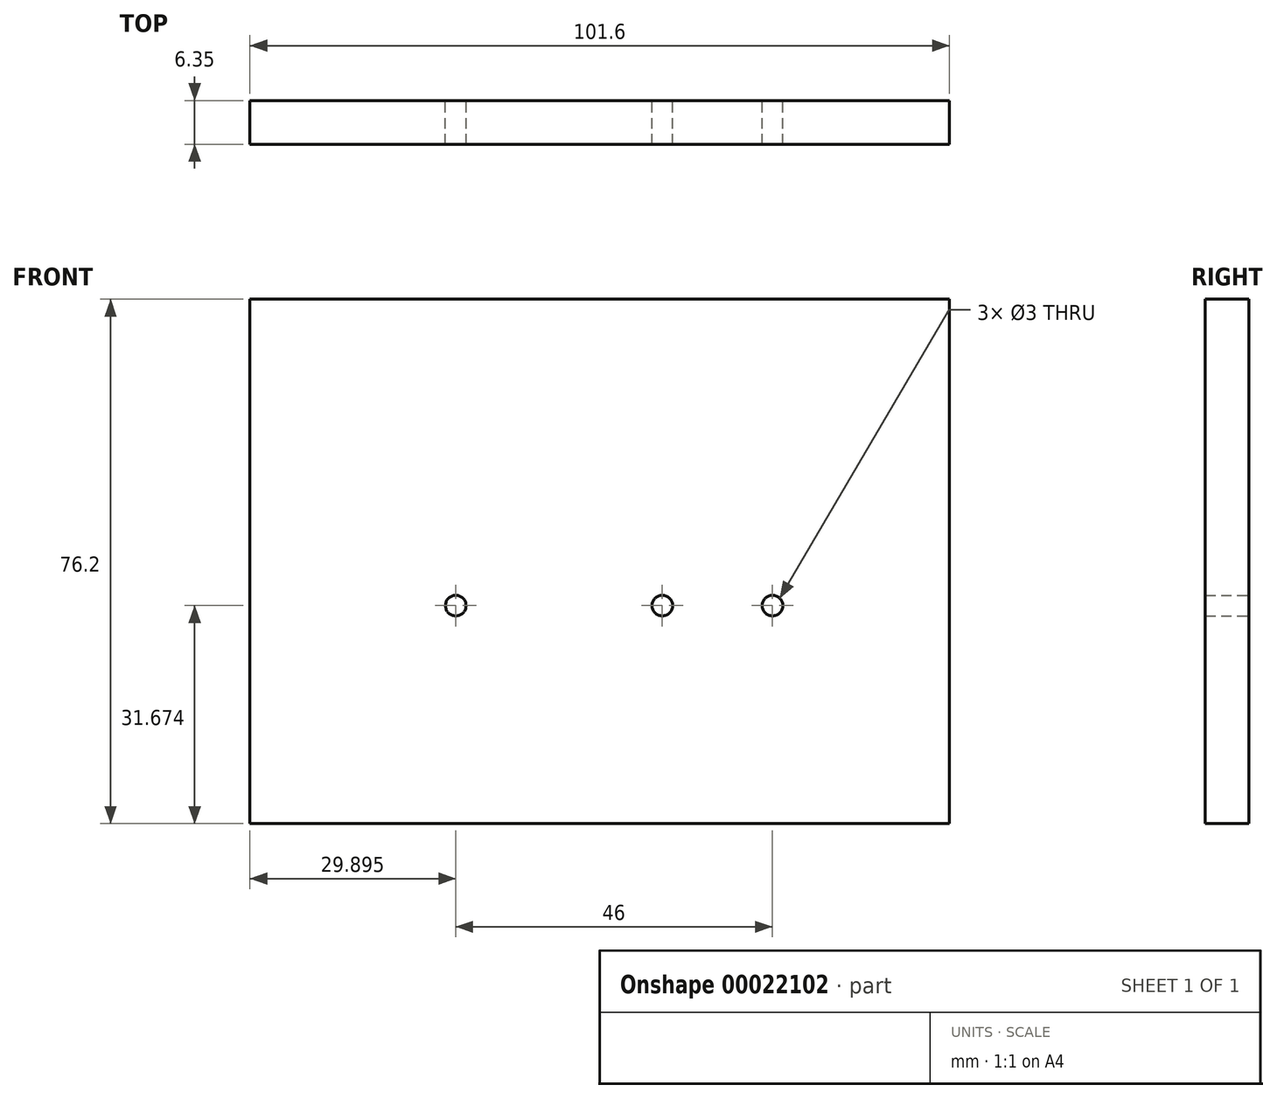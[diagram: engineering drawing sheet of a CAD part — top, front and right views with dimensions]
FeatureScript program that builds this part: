
annotation { "Feature Type Name" : "Feature", "Feature Type Description" : "" }
export const myFeature = defineFeature(function(context is Context, id is Id, definition is map)
    precondition{}
    {
        {
            var Q0;
            Q0=qCreatedBy(makeId("Front.planeOp"),FACE);
            var sketch = newSketch(context, id + "F0", { "sketchPlane" : qUnion([Q0])});
            skLineSegment(sketch, "E0.bottom", {"start": v(-44.9, 85) * mm, "end": v(56.7, 85) * mm});
            skLineSegment(sketch, "E0.top", {"start": v(-44.9, 8.8) * mm, "end": v(56.7, 8.8) * mm});
            skLineSegment(sketch, "E0.left", {"start": v(-44.9, 85) * mm, "end": v(-44.9, 8.8) * mm});
            skLineSegment(sketch, "E0.right", {"start": v(56.7, 85) * mm, "end": v(56.7, 8.8) * mm});
            skLineSegment(sketch, "E1", {"start": v(-15, 40.48) * mm, "end": v(31, 40.48) * mm});
            skLineSegment(sketch, "E2", {"start": v(15, 40.48) * mm, "end": v(31, 40.48) * mm});
            skCircle(sketch, "E3", {"center": v(-15, 40.48) * mm, "radius": 1.5 * mm});
            skCircle(sketch, "E4", {"center": v(15, 40.48) * mm, "radius": 1.5 * mm});
            skCircle(sketch, "E5", {"center": v(31, 40.48) * mm, "radius": 1.5 * mm});
            skSolve(sketch);
        }
        {
            var Q0;
            Q0=makeQuery(id+"F0.imprint","IMPRINT",FACE,{"disambiguationData":[TD([[makeQuery(id+"F0.imprint","IMPRINT",EDGE,{"derivedFrom":sQuery(id+"F0.wireOp",EDGE,"E0.bottom")}),-1.0]])]});
            extrude(context, id + "F1", {"entities" : qUnion([Q0]), "depth" : 6.35 * mm});
        }
    });
